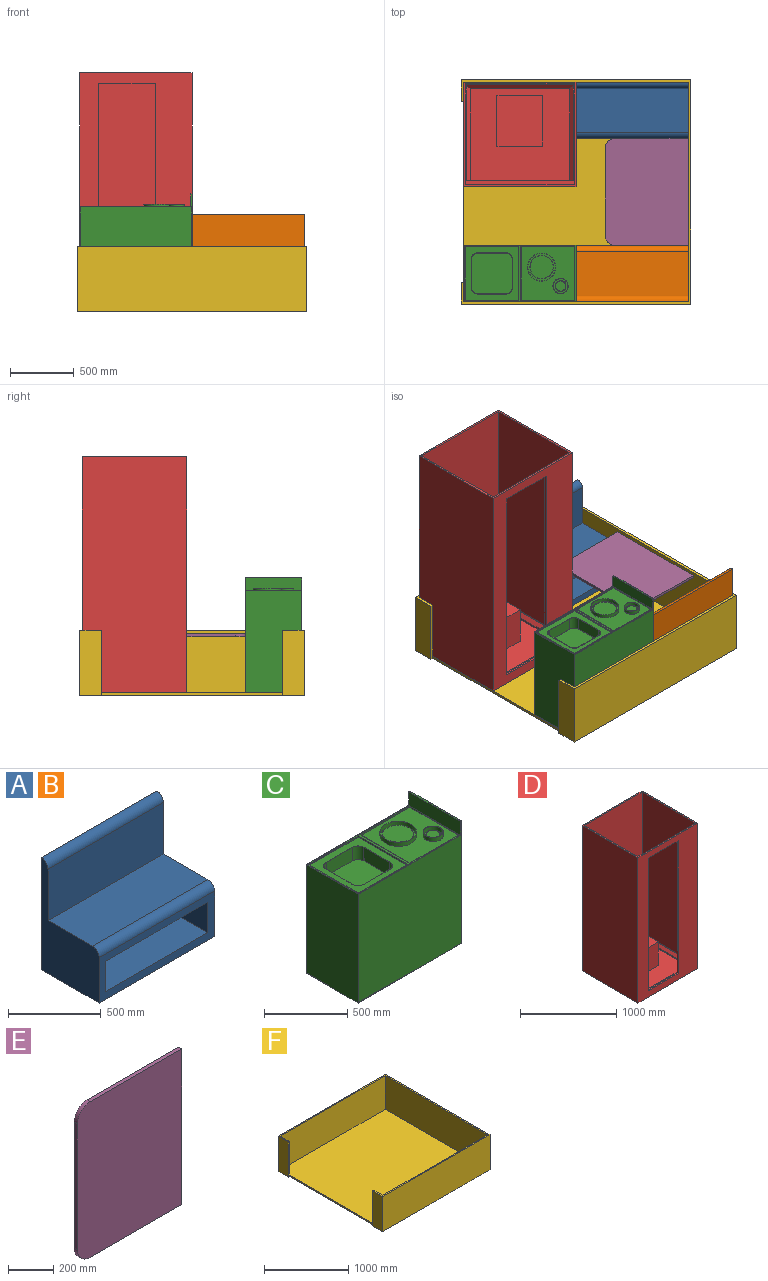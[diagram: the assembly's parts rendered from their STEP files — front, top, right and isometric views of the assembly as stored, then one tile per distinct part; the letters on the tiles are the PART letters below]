
ASSEMBLY  parts=6 mates=5
PART A: 14 faces, bbox 880x440x740 mm
  f0: plane 880x300mm, normal (0,-1,0), area 108000mm2, adj f1,f2,f3,f5,f6,f7,f8,f12
  f1: plane 740x440mm, normal (-1,0,0), area 172427mm2, adj f0,f2,f4,f10,f11,f12,f13
  f2: plane 880x440mm, normal (0,0,-1), area 387200mm2, adj f0,f1,f3,f4
  f3: plane 740x440mm, normal (1,0,0), area 172427mm2, adj f0,f2,f4,f10,f11,f12,f13
  f4: plane 880x740mm, normal (0,1,0), area 651200mm2, adj f1,f2,f3,f13
  f5: plane 390x200mm, normal (1,0,0), area 78000mm2, adj f0,f6,f8,f9
  f6: plane 780x390mm, normal (0,0,1), area 304200mm2, adj f0,f5,f7,f9
  f7: plane 390x200mm, normal (-1,0,0), area 78000mm2, adj f0,f6,f8,f9
  f8: plane 780x390mm, normal (0,0,-1), area 304200mm2, adj f0,f5,f7,f9
  f9: plane 780x200mm, normal (0,-1,0), area 156000mm2, adj f5,f6,f7,f8
  f10: plane 880x340mm, normal (0,-1,0), area 299200mm2, adj f1,f3,f11,f13
  f11: plane 880x340mm, normal (0,0,1), area 299200mm2, adj f1,f3,f10,f12
  f12: cylinder r=50mm len=880mm, axis (1,0,0), area 69115mm2, adj f0,f1,f3,f11
  f13: cylinder r=50mm len=880mm, axis (-1,0,0), area 69115mm2, adj f1,f3,f4,f10
PART B: same geometry as A
PART C: 195 faces, bbox 880x440x900 mm
  f0: plane 420x420mm, normal (0,0,1), area 76146mm2, adj f7,f8,f9,f10,f16,f17,f18,f19
  f1: plane 870x440mm, normal (0,0,1), area 30000mm2, adj f2,f5,f6,f7,f8,f9,f10,f11
  f2: plane 800x440mm, normal (-1,0,0), area 352000mm2, adj f1,f3,f5,f6
  f3: plane 880x440mm, normal (0,0,-1), area 387200mm2, adj f2,f4,f5,f6
  f4: plane 900x440mm, normal (1,0,0), area 396000mm2, adj f3,f5,f6,f194
  f5: plane 900x880mm, normal (0,-1,0), area 705000mm2, adj f1,f2,f3,f4,f11,f194
  f6: plane 900x880mm, normal (0,1,0), area 429384.1mm2, adj f1,f2,f3,f4,f11,f29,f30,f31
  f7: plane 420x10mm, normal (0,-1,0), area 4200mm2, adj f0,f1,f8,f10
  f8: plane 420x10mm, normal (1,0,0), area 4200mm2, adj f0,f1,f7,f9
  f9: plane 420x10mm, normal (0,1,0), area 4200mm2, adj f0,f1,f8,f10
  f10: plane 420x10mm, normal (-1,0,0), area 4200mm2, adj f0,f1,f7,f9
  f11: plane 440x110mm, normal (-1,0,0), area 48200mm2, adj f1,f5,f6,f12,f14,f15,f194
  f12: plane 420x10mm, normal (0,-1,0), area 4200mm2, adj f1,f11,f13,f15
  f13: plane 420x10mm, normal (1,0,0), area 4200mm2, adj f1,f12,f14,f15
  f14: plane 420x10mm, normal (0,1,0), area 4200mm2, adj f1,f11,f13,f15
  f15: plane 420x420mm, normal (0,0,1), area 127077mm2, adj f11,f12,f13,f14,f25,f27
  f16: plane 220x100mm, normal (-1,0,0), area 22000mm2, adj f0,f17,f23,f24
  f17: cylinder r=50mm len=100mm, axis (0,0,1), area 7854mm2, adj f0,f16,f18,f24
  f18: plane 220x100mm, normal (0,-1,0), area 22000mm2, adj f0,f17,f19,f24
  f19: cylinder r=50mm len=100mm, axis (0,0,1), area 7854mm2, adj f0,f18,f20,f24
  f20: plane 220x100mm, normal (1,0,0), area 22000mm2, adj f0,f19,f21,f24
  f21: cylinder r=50mm len=100mm, axis (0,0,1), area 7854mm2, adj f0,f20,f22,f24
  f22: plane 220x100mm, normal (0,1,0), area 22000mm2, adj f0,f21,f23,f24
  f23: cylinder r=50mm len=100mm, axis (0,0,1), area 7854mm2, adj f0,f16,f22,f24
  f24: plane 320x320mm, normal (0,0,1), area 100254mm2, adj f16,f17,f18,f19,f20,f21,f22,f23
  f25: cylinder r=60mm len=120mm, axis (0,0,-1), area 11309.7mm2, adj f15,f26
  f26: plane 120x120mm, normal (0,0,1), area 937.3mm2, adj f25,f123
  f27: cylinder r=110mm len=220mm, axis (0,0,-1), area 20734.5mm2, adj f15,f28
  f28: plane 220x220mm, normal (0,0,1), area 1735.3mm2, adj f27,f124
  f29: cylinder r=50mm len=50mm, axis (0,1,0), area 1570.8mm2, adj f6,f30,f36,f37
  f30: plane 145x20mm, normal (1,0,0), area 2900mm2, adj f6,f29,f31,f37
  f31: cylinder r=50mm len=50mm, axis (0,1,0), area 1570.8mm2, adj f6,f30,f32,f37
  f32: plane 190x20mm, normal (0,0,1), area 3800mm2, adj f6,f31,f33,f37
  f33: cylinder r=50mm len=50mm, axis (0,1,0), area 1570.8mm2, adj f6,f32,f34,f37
  f34: plane 145x20mm, normal (-1,0,0), area 2900mm2, adj f6,f33,f35,f37
  f35: cylinder r=50mm len=50mm, axis (0,1,0), area 1570.8mm2, adj f6,f34,f36,f37
  f36: plane 190x20mm, normal (0,0,-1), area 3800mm2, adj f6,f29,f35,f37
  f37: plane 410x365mm, normal (0,-1,0), area 80746mm2, adj f29,f30,f31,f32,f33,f34,f35,f36
  f38: plane 180x180mm, normal (0,0,-1), area 25446.9mm2, adj f40
  f39: plane 80x80mm, normal (0,0,-1), area 5026.5mm2, adj f41
  f40: cylinder r=90mm len=180mm, axis (0,0,-1), area 16964.6mm2, adj f38,f46
  f41: cylinder r=40mm len=80mm, axis (0,0,-1), area 7539.8mm2, adj f39,f46
  f42: plane 410x365mm, normal (0,1,0), area 149650mm2, adj f43,f44,f45,f46
  f43: plane 400x365mm, normal (1,0,0), area 146000mm2, adj f37,f42,f45,f46
  f44: plane 400x365mm, normal (-1,0,0), area 146000mm2, adj f37,f42,f45,f46
  f45: plane 410x400mm, normal (0,0,1), area 164000mm2, adj f37,f42,f43,f44
  f46: plane 410x400mm, normal (0,0,-1), area 133526.6mm2, adj f37,f40,f41,f42,f43,f44
  f47: cylinder r=50mm len=50mm, axis (0,1,0), area 1570.8mm2, adj f6,f48,f54,f55
  f48: plane 145x20mm, normal (1,0,0), area 2900mm2, adj f6,f47,f49,f55
  f49: cylinder r=50mm len=50mm, axis (0,1,0), area 1570.8mm2, adj f6,f48,f50,f55
  f50: plane 190x20mm, normal (0,0,1), area 3800mm2, adj f6,f49,f51,f55
  f51: cylinder r=50mm len=50mm, axis (0,1,0), area 1570.8mm2, adj f6,f50,f52,f55
  f52: plane 145x20mm, normal (-1,0,0), area 2900mm2, adj f6,f51,f53,f55
  f53: cylinder r=50mm len=50mm, axis (0,1,0), area 1570.8mm2, adj f6,f52,f54,f55
  f54: plane 190x20mm, normal (0,0,-1), area 3800mm2, adj f6,f47,f53,f55
  f55: plane 410x365mm, normal (0,-1,0), area 80746mm2, adj f47,f48,f49,f50,f51,f52,f53,f54
  f56: plane 360x360mm, normal (0,0,-1), area 125393.8mm2, adj f57,f58,f59,f60,f61,f62,f63,f64
  f57: plane 220x100mm, normal (1,0,0), area 22000mm2, adj f56,f58,f64,f68
  f58: cylinder r=70mm len=100mm, axis (0,0,1), area 10995.6mm2, adj f56,f57,f59,f68
  f59: plane 220x100mm, normal (0,-1,0), area 22000mm2, adj f56,f58,f60,f68
  f60: cylinder r=70mm len=100mm, axis (0,0,1), area 10995.6mm2, adj f56,f59,f61,f68
  f61: plane 220x100mm, normal (-1,0,0), area 22000mm2, adj f56,f60,f62,f68
  f62: cylinder r=70mm len=100mm, axis (0,0,1), area 10995.6mm2, adj f56,f61,f63,f68
  f63: plane 220x100mm, normal (0,1,0), area 22000mm2, adj f56,f62,f64,f68
  f64: cylinder r=70mm len=100mm, axis (0,0,1), area 10995.6mm2, adj f56,f57,f63,f68
  f65: plane 410x365mm, normal (0,1,0), area 149650mm2, adj f66,f67,f68,f69
  f66: plane 400x365mm, normal (-1,0,0), area 146000mm2, adj f55,f65,f67,f68
  f67: plane 410x400mm, normal (0,0,1), area 164000mm2, adj f55,f65,f66,f69
  f68: plane 410x400mm, normal (0,0,-1), area 38606.2mm2, adj f55,f57,f58,f59,f60,f61,f62,f63
  f69: plane 400x365mm, normal (1,0,0), area 146000mm2, adj f55,f65,f67,f68
  f70: cylinder r=50mm len=50mm, axis (0,1,0), area 1570.8mm2, adj f6,f71,f77,f78
  f71: plane 145x20mm, normal (1,0,0), area 2900mm2, adj f6,f70,f72,f78
  f72: cylinder r=50mm len=50mm, axis (0,1,0), area 1570.8mm2, adj f6,f71,f73,f78
  f73: plane 190x20mm, normal (0,0,1), area 3800mm2, adj f6,f72,f74,f78
  f74: cylinder r=50mm len=50mm, axis (0,1,0), area 1570.8mm2, adj f6,f73,f75,f78
  f75: plane 145x20mm, normal (-1,0,0), area 2900mm2, adj f6,f74,f76,f78
  f76: cylinder r=50mm len=50mm, axis (0,1,0), area 1570.8mm2, adj f6,f75,f77,f78
  f77: plane 190x20mm, normal (0,0,-1), area 3800mm2, adj f6,f70,f76,f78
  f78: plane 410x365mm, normal (0,-1,0), area 80746mm2, adj f70,f71,f72,f73,f74,f75,f76,f77
  f79: plane 410x365mm, normal (0,1,0), area 149650mm2, adj f80,f81,f82,f83
  f80: plane 400x365mm, normal (1,0,0), area 146000mm2, adj f78,f79,f82,f83
  f81: plane 400x365mm, normal (-1,0,0), area 146000mm2, adj f78,f79,f82,f83
  f82: plane 410x400mm, normal (0,0,-1), area 164000mm2, adj f78,f79,f80,f81
  f83: plane 410x400mm, normal (0,0,1), area 164000mm2, adj f78,f79,f80,f81
  f84: cylinder r=50mm len=50mm, axis (0,1,0), area 1570.8mm2, adj f6,f85,f91,f92
  f85: plane 145x20mm, normal (-1,0,0), area 2900mm2, adj f6,f84,f86,f92
  f86: cylinder r=50mm len=50mm, axis (0,1,0), area 1570.8mm2, adj f6,f85,f87,f92
  f87: plane 190x20mm, normal (0,0,-1), area 3800mm2, adj f6,f86,f88,f92
  f88: cylinder r=50mm len=50mm, axis (0,1,0), area 1570.8mm2, adj f6,f87,f89,f92
  f89: plane 145x20mm, normal (1,0,0), area 2900mm2, adj f6,f88,f90,f92
  f90: cylinder r=50mm len=50mm, axis (0,1,0), area 1570.8mm2, adj f6,f89,f91,f92
  f91: plane 190x20mm, normal (0,0,1), area 3800mm2, adj f6,f84,f90,f92
  f92: plane 410x365mm, normal (0,-1,0), area 80746mm2, adj f84,f85,f86,f87,f88,f89,f90,f91
  f93: plane 410x365mm, normal (0,1,0), area 149650mm2, adj f94,f95,f96,f97
  f94: plane 400x365mm, normal (-1,0,0), area 146000mm2, adj f92,f93,f95,f96
  f95: plane 410x400mm, normal (0,0,-1), area 164000mm2, adj f92,f93,f94,f97
  f96: plane 410x400mm, normal (0,0,1), area 164000mm2, adj f92,f93,f94,f97
  f97: plane 400x365mm, normal (1,0,0), area 146000mm2, adj f92,f93,f95,f96
  f98: plane 425.08x425.08mm, normal (0,0,-1), area 77385.6mm2, adj f105,f106,f107,f108,f114,f115,f116,f117
  f99: plane 874.92x434.92mm, normal (0,0,-1), area 19134.2mm2, adj f100,f102,f103,f104,f105,f106,f107,f108
  f100: plane 794.92x434.92mm, normal (1,0,0), area 345726.6mm2, adj f99,f101,f103,f104
  f101: plane 874.92x434.92mm, normal (0,0,1), area 380520.2mm2, adj f100,f102,f103,f104
  f102: plane 794.92x434.92mm, normal (-1,0,0), area 345726.6mm2, adj f99,f101,f103,f104
  f103: plane 874.92x794.92mm, normal (0,1,0), area 695491.4mm2, adj f99,f100,f101,f102
  f104: plane 874.92x794.92mm, normal (0,-1,0), area 409795.3mm2, adj f99,f100,f101,f102,f125,f126,f127,f128
  f105: plane 425.08x10mm, normal (0,1,0), area 4250.8mm2, adj f98,f99,f106,f108
  f106: plane 425.08x10mm, normal (-1,0,0), area 4250.8mm2, adj f98,f99,f105,f107
  f107: plane 425.08x10mm, normal (0,-1,0), area 4250.8mm2, adj f98,f99,f106,f108
  f108: plane 425.08x10mm, normal (1,0,0), area 4250.8mm2, adj f98,f99,f105,f107
  f109: plane 425.08x10mm, normal (1,0,0), area 4250.8mm2, adj f99,f110,f112,f113
  f110: plane 425.08x10mm, normal (0,1,0), area 4250.8mm2, adj f99,f109,f111,f113
  f111: plane 425.08x10mm, normal (-1,0,0), area 4250.8mm2, adj f99,f110,f112,f113
  f112: plane 425.08x10mm, normal (0,-1,0), area 4250.8mm2, adj f99,f109,f111,f113
  f113: plane 425.08x425.08mm, normal (0,0,-1), area 134042.5mm2, adj f109,f110,f111,f112,f123,f124
  f114: plane 220x100mm, normal (1,0,0), area 22000mm2, adj f98,f115,f121,f122
  f115: cylinder r=52.54mm len=100mm, axis (0,0,1), area 8253mm2, adj f98,f114,f116,f122
  f116: plane 220x100mm, normal (0,1,0), area 22000mm2, adj f98,f115,f117,f122
  f117: cylinder r=52.54mm len=100mm, axis (0,0,1), area 8253mm2, adj f98,f116,f118,f122
  f118: plane 220x100mm, normal (-1,0,0), area 22000mm2, adj f98,f117,f119,f122
  f119: cylinder r=52.54mm len=100mm, axis (0,0,1), area 8253mm2, adj f98,f118,f120,f122
  f120: plane 220x100mm, normal (0,-1,0), area 22000mm2, adj f98,f119,f121,f122
  f121: cylinder r=52.54mm len=100mm, axis (0,0,1), area 8253mm2, adj f98,f114,f120,f122
  f122: plane 325.08x325.08mm, normal (0,0,-1), area 103307.4mm2, adj f114,f115,f116,f117,f118,f119,f120,f121
  f123: cylinder r=57.46mm len=114.92mm, axis (0,0,-1), area 11748mm2, adj f26,f113
  f124: cylinder r=107.46mm len=214.92mm, axis (0,0,-1), area 21970.7mm2, adj f28,f113
  f125: cylinder r=52.54mm len=52.54mm, axis (0,1,0), area 1231.3mm2, adj f104,f126,f132,f133
  f126: plane 145x14.92mm, normal (-1,0,0), area 2163.4mm2, adj f104,f125,f127,f133
  f127: cylinder r=52.54mm len=52.54mm, axis (0,1,0), area 1231.3mm2, adj f104,f126,f128,f133
  f128: plane 190x14.92mm, normal (0,0,-1), area 2834.8mm2, adj f104,f127,f129,f133
  f129: cylinder r=52.54mm len=52.54mm, axis (0,1,0), area 1231.3mm2, adj f104,f128,f130,f133
  f130: plane 145x14.92mm, normal (1,0,0), area 2163.4mm2, adj f104,f129,f131,f133
  f131: cylinder r=52.54mm len=52.54mm, axis (0,1,0), area 1231.3mm2, adj f104,f130,f132,f133
  f132: plane 190x14.92mm, normal (0,0,1), area 2834.8mm2, adj f104,f125,f131,f133
  f133: plane 415.08x370.08mm, normal (0,1,0), area 82188.8mm2, adj f125,f126,f127,f128,f129,f130,f131,f132
  f134: plane 185.08x185.08mm, normal (0,0,1), area 26903.5mm2, adj f136
  f135: plane 85.08x85.08mm, normal (0,0,1), area 5685.2mm2, adj f137
  f136: cylinder r=92.54mm len=185.08mm, axis (0,0,-1), area 17443.4mm2, adj f134,f142
  f137: cylinder r=42.54mm len=85.08mm, axis (0,0,-1), area 8018.6mm2, adj f135,f142
  f138: plane 415.08x370.08mm, normal (0,-1,0), area 153612.8mm2, adj f139,f140,f141,f142
  f139: plane 405.08x370.08mm, normal (-1,0,0), area 149912mm2, adj f133,f138,f141,f142
  f140: plane 405.08x370.08mm, normal (1,0,0), area 149912mm2, adj f133,f138,f141,f142
  f141: plane 415.08x405.08mm, normal (0,0,-1), area 168140.6mm2, adj f133,f138,f139,f140
  f142: plane 415.08x405.08mm, normal (0,0,1), area 135551.9mm2, adj f133,f136,f137,f138,f139,f140
  f143: cylinder r=52.54mm len=52.54mm, axis (0,1,0), area 1231.3mm2, adj f104,f144,f150,f151
  f144: plane 145x14.92mm, normal (-1,0,0), area 2163.4mm2, adj f104,f143,f145,f151
  f145: cylinder r=52.54mm len=52.54mm, axis (0,1,0), area 1231.3mm2, adj f104,f144,f146,f151
  f146: plane 190x14.92mm, normal (0,0,-1), area 2834.8mm2, adj f104,f145,f147,f151
  f147: cylinder r=52.54mm len=52.54mm, axis (0,1,0), area 1231.3mm2, adj f104,f146,f148,f151
  f148: plane 145x14.92mm, normal (1,0,0), area 2163.4mm2, adj f104,f147,f149,f151
  f149: cylinder r=52.54mm len=52.54mm, axis (0,1,0), area 1231.3mm2, adj f104,f148,f150,f151
  f150: plane 190x14.92mm, normal (0,0,1), area 2834.8mm2, adj f104,f143,f149,f151
  f151: plane 415.08x370.08mm, normal (0,1,0), area 82188.8mm2, adj f143,f144,f145,f146,f147,f148,f149,f150
  f152: plane 354.92x354.92mm, normal (0,0,1), area 122061.7mm2, adj f153,f154,f155,f156,f157,f158,f159,f160
  f153: plane 220x100mm, normal (-1,0,0), area 22000mm2, adj f152,f154,f160,f164
  f154: cylinder r=67.46mm len=100mm, axis (0,0,1), area 10596.6mm2, adj f152,f153,f155,f164
  f155: plane 220x100mm, normal (0,1,0), area 22000mm2, adj f152,f154,f156,f164
  f156: cylinder r=67.46mm len=100mm, axis (0,0,1), area 10596.6mm2, adj f152,f155,f157,f164
  f157: plane 220x100mm, normal (1,0,0), area 22000mm2, adj f152,f156,f158,f164
  f158: cylinder r=67.46mm len=100mm, axis (0,0,1), area 10596.6mm2, adj f152,f157,f159,f164
  f159: plane 220x100mm, normal (0,-1,0), area 22000mm2, adj f152,f158,f160,f164
  f160: cylinder r=67.46mm len=100mm, axis (0,0,1), area 10596.6mm2, adj f152,f153,f159,f164
  f161: plane 415.08x370.08mm, normal (0,-1,0), area 153612.8mm2, adj f162,f163,f164,f165
  f162: plane 405.08x370.08mm, normal (1,0,0), area 149912mm2, adj f151,f161,f163,f164
  f163: plane 415.08x405.08mm, normal (0,0,-1), area 168140.6mm2, adj f151,f161,f162,f165
  f164: plane 415.08x405.08mm, normal (0,0,1), area 46078.9mm2, adj f151,f153,f154,f155,f156,f157,f158,f159
  f165: plane 405.08x370.08mm, normal (-1,0,0), area 149912mm2, adj f151,f161,f163,f164
  f166: cylinder r=52.54mm len=52.54mm, axis (0,1,0), area 1231.3mm2, adj f104,f167,f173,f174
  f167: plane 145x14.92mm, normal (-1,0,0), area 2163.4mm2, adj f104,f166,f168,f174
  f168: cylinder r=52.54mm len=52.54mm, axis (0,1,0), area 1231.3mm2, adj f104,f167,f169,f174
  f169: plane 190x14.92mm, normal (0,0,-1), area 2834.8mm2, adj f104,f168,f170,f174
  f170: cylinder r=52.54mm len=52.54mm, axis (0,1,0), area 1231.3mm2, adj f104,f169,f171,f174
  f171: plane 145x14.92mm, normal (1,0,0), area 2163.4mm2, adj f104,f170,f172,f174
  f172: cylinder r=52.54mm len=52.54mm, axis (0,1,0), area 1231.3mm2, adj f104,f171,f173,f174
  f173: plane 190x14.92mm, normal (0,0,1), area 2834.8mm2, adj f104,f166,f172,f174
  f174: plane 415.08x370.08mm, normal (0,1,0), area 82188.8mm2, adj f166,f167,f168,f169,f170,f171,f172,f173
  f175: plane 415.08x370.08mm, normal (0,-1,0), area 153612.8mm2, adj f176,f177,f178,f179
  f176: plane 405.08x370.08mm, normal (-1,0,0), area 149912mm2, adj f174,f175,f178,f179
  f177: plane 405.08x370.08mm, normal (1,0,0), area 149912mm2, adj f174,f175,f178,f179
  f178: plane 415.08x405.08mm, normal (0,0,1), area 168140.6mm2, adj f174,f175,f176,f177
  f179: plane 415.08x405.08mm, normal (0,0,-1), area 168140.6mm2, adj f174,f175,f176,f177
  f180: cylinder r=52.54mm len=52.54mm, axis (0,1,0), area 1231.3mm2, adj f104,f181,f187,f188
  f181: plane 145x14.92mm, normal (1,0,0), area 2163.4mm2, adj f104,f180,f182,f188
  f182: cylinder r=52.54mm len=52.54mm, axis (0,1,0), area 1231.3mm2, adj f104,f181,f183,f188
  f183: plane 190x14.92mm, normal (0,0,1), area 2834.8mm2, adj f104,f182,f184,f188
  f184: cylinder r=52.54mm len=52.54mm, axis (0,1,0), area 1231.3mm2, adj f104,f183,f185,f188
  f185: plane 145x14.92mm, normal (-1,0,0), area 2163.4mm2, adj f104,f184,f186,f188
  f186: cylinder r=52.54mm len=52.54mm, axis (0,1,0), area 1231.3mm2, adj f104,f185,f187,f188
  f187: plane 190x14.92mm, normal (0,0,-1), area 2834.8mm2, adj f104,f180,f186,f188
  f188: plane 415.08x370.08mm, normal (0,1,0), area 82188.8mm2, adj f180,f181,f182,f183,f184,f185,f186,f187
  f189: plane 415.08x370.08mm, normal (0,-1,0), area 153612.8mm2, adj f190,f191,f192,f193
  f190: plane 405.08x370.08mm, normal (1,0,0), area 149912mm2, adj f188,f189,f191,f192
  f191: plane 415.08x405.08mm, normal (0,0,1), area 168140.6mm2, adj f188,f189,f190,f193
  f192: plane 415.08x405.08mm, normal (0,0,-1), area 168140.6mm2, adj f188,f189,f190,f193
  f193: plane 405.08x370.08mm, normal (-1,0,0), area 149912mm2, adj f188,f189,f191,f192
  f194: plane 440x10mm, normal (0,0,1), area 4400mm2, adj f4,f5,f6,f11
PART D: 28 faces, bbox 880x820x1850 mm
  f0: plane 1795x850mm, normal (0,1,0), area 782150mm2, adj f2,f4,f9,f10,f19,f20,f21,f22
  f1: plane 1850x880mm, normal (0,-1,0), area 884400mm2, adj f4,f5,f6,f7,f19,f20,f21,f22
  f2: plane 850x790mm, normal (0,0,1), area 41500mm2, adj f0,f3,f9,f10,f13,f16,f17,f18
  f3: plane 1795x850mm, normal (0,-1,0), area 1525750mm2, adj f2,f4,f9,f10
  f4: plane 880x820mm, normal (0,0,1), area 50100mm2, adj f0,f1,f3,f5,f7,f8,f9,f10
  f5: plane 1850x820mm, normal (-1,0,0), area 1517000mm2, adj f1,f4,f6,f8
  f6: plane 880x820mm, normal (0,0,-1), area 721600mm2, adj f1,f5,f7,f8
  f7: plane 1850x820mm, normal (1,0,0), area 1517000mm2, adj f1,f4,f6,f8
  f8: plane 1850x880mm, normal (0,1,0), area 1628000mm2, adj f4,f5,f6,f7
  f9: plane 1795x790mm, normal (1,0,0), area 1418050mm2, adj f0,f2,f3,f4
  f10: plane 1795x790mm, normal (-1,0,0), area 1418050mm2, adj f0,f2,f3,f4
  f11: plane 720x15mm, normal (1,0,0), area 10800mm2, adj f13,f14,f15,f16
  f12: plane 720x15mm, normal (-1,0,0), area 10800mm2, adj f13,f14,f15,f18
  f13: plane 840x45mm, normal (0,1,0), area 36000mm2, adj f2,f11,f12,f15,f16,f18
  f14: plane 780x15mm, normal (0,-1,0), area 11700mm2, adj f11,f12,f15,f17
  f15: plane 780x720mm, normal (0,0,1), area 417600mm2, adj f11,f12,f13,f14,f23,f24,f25,f26
  f16: plane 750x30mm, normal (0.71,0,0.71), area 31183.4mm2, adj f2,f11,f13,f17
  f17: plane 840x30mm, normal (0,-0.71,0.71), area 34365.4mm2, adj f2,f14,f16,f18
  f18: plane 750x30mm, normal (-0.71,0,0.71), area 31183.4mm2, adj f2,f12,f13,f17
  f19: plane 440x15mm, normal (0,0,-1), area 6600mm2, adj f0,f1,f20,f22
  f20: plane 1690x15mm, normal (1,0,0), area 25350mm2, adj f0,f1,f19,f21
  f21: plane 440x15mm, normal (0,0,1), area 6600mm2, adj f0,f1,f20,f22
  f22: plane 1690x15mm, normal (-1,0,0), area 25350mm2, adj f0,f1,f19,f21
  f23: plane 400x300mm, normal (1,0,0), area 120000mm2, adj f15,f24,f26,f27
  f24: plane 360x300mm, normal (0,1,0), area 108000mm2, adj f15,f23,f25,f27
  f25: plane 400x300mm, normal (-1,0,0), area 120000mm2, adj f15,f24,f26,f27
  f26: plane 360x300mm, normal (0,-1,0), area 108000mm2, adj f15,f23,f25,f27
  f27: plane 400x360mm, normal (0,0,1), area 144000mm2, adj f23,f24,f25,f26
PART E: 8 faces, bbox 650x20x840 mm
  f0: plane 680x20mm, normal (-1,0,0), area 13600mm2, adj f4,f5,f6,f7
  f1: plane 570x20mm, normal (0,0,-1), area 11400mm2, adj f2,f4,f5,f6
  f2: plane 840x20mm, normal (1,0,0), area 16800mm2, adj f1,f3,f4,f5
  f3: plane 570x20mm, normal (0,0,1), area 11400mm2, adj f2,f4,f5,f7
  f4: plane 840x650mm, normal (0,-1,0), area 543253.1mm2, adj f0,f1,f2,f3,f6,f7
  f5: plane 840x650mm, normal (0,1,0), area 543253.1mm2, adj f0,f1,f2,f3,f6,f7
  f6: cylinder r=80mm len=80mm, axis (0,-1,0), area 2513.3mm2, adj f0,f1,f4,f5
  f7: cylinder r=80mm len=80mm, axis (0,1,0), area 2513.3mm2, adj f0,f3,f4,f5
PART F: 16 faces, bbox 1800x1760x510 mm
  f0: plane 1420x20mm, normal (-1,0,0), area 28400mm2, adj f2,f6,f11,f14
  f1: plane 1800x1760mm, normal (0,0,1), area 112400mm2, adj f3,f4,f5,f7,f8,f9,f10,f11
  f2: plane 1800x1760mm, normal (0,0,-1), area 3139600mm2, adj f0,f3,f4,f5,f11,f12,f14,f15
  f3: plane 1760x510mm, normal (1,0,0), area 897600mm2, adj f1,f2,f4,f5
  f4: plane 1800x510mm, normal (0,-1,0), area 918000mm2, adj f1,f2,f3,f15
  f5: plane 1800x510mm, normal (0,1,0), area 918000mm2, adj f1,f2,f3,f12
  f6: plane 1760x1720mm, normal (0,0,1), area 3027200mm2, adj f0,f7,f8,f9,f10,f13
  f7: plane 1720x490mm, normal (-1,0,0), area 842800mm2, adj f1,f6,f8,f9
  f8: plane 1760x490mm, normal (0,1,0), area 862400mm2, adj f1,f6,f7,f13
  f9: plane 1760x490mm, normal (0,-1,0), area 862400mm2, adj f1,f6,f7,f10
  f10: plane 490x150mm, normal (1,0,0), area 73500mm2, adj f1,f6,f9,f11
  f11: plane 510x20mm, normal (0,-1,0), area 10200mm2, adj f0,f1,f2,f10,f12
  f12: plane 510x170mm, normal (-1,0,0), area 86700mm2, adj f1,f2,f5,f11
  f13: plane 490x150mm, normal (1,0,0), area 73500mm2, adj f1,f6,f8,f14
  f14: plane 510x20mm, normal (0,1,0), area 10200mm2, adj f0,f1,f2,f13,f15
  f15: plane 510x170mm, normal (-1,0,0), area 86700mm2, adj f1,f2,f4,f14
PLACE A t=(880,1740,-450)mm
PLACE B rot(axis=(0,0,1),180deg) t=(1760,20,-450)mm
PLACE C t=(0,460,-450)mm
PLACE D t=(0,1740,-450)mm
PLACE E rot(axis=(-1,0,0),90deg) t=(1110,460,-10)mm
PLACE F t=(0,1740,-450)mm
MATE fastened C.f3 <-> F.f6  axis (0,0,-1) through (0,20,-450)mm
MATE fastened A.f2 <-> F.f6  axis (0,0,-1) through (1760,1740,-450)mm
MATE fastened B.f2 <-> F.f6  axis (0,0,-1) through (1760,20,-450)mm
MATE fastened E.f2 <-> F.f7  axis (1,0,0) through (1760,460,-10)mm
MATE fastened D.f6 <-> F.f6  axis (0,0,-1) through (0,1740,-450)mm
